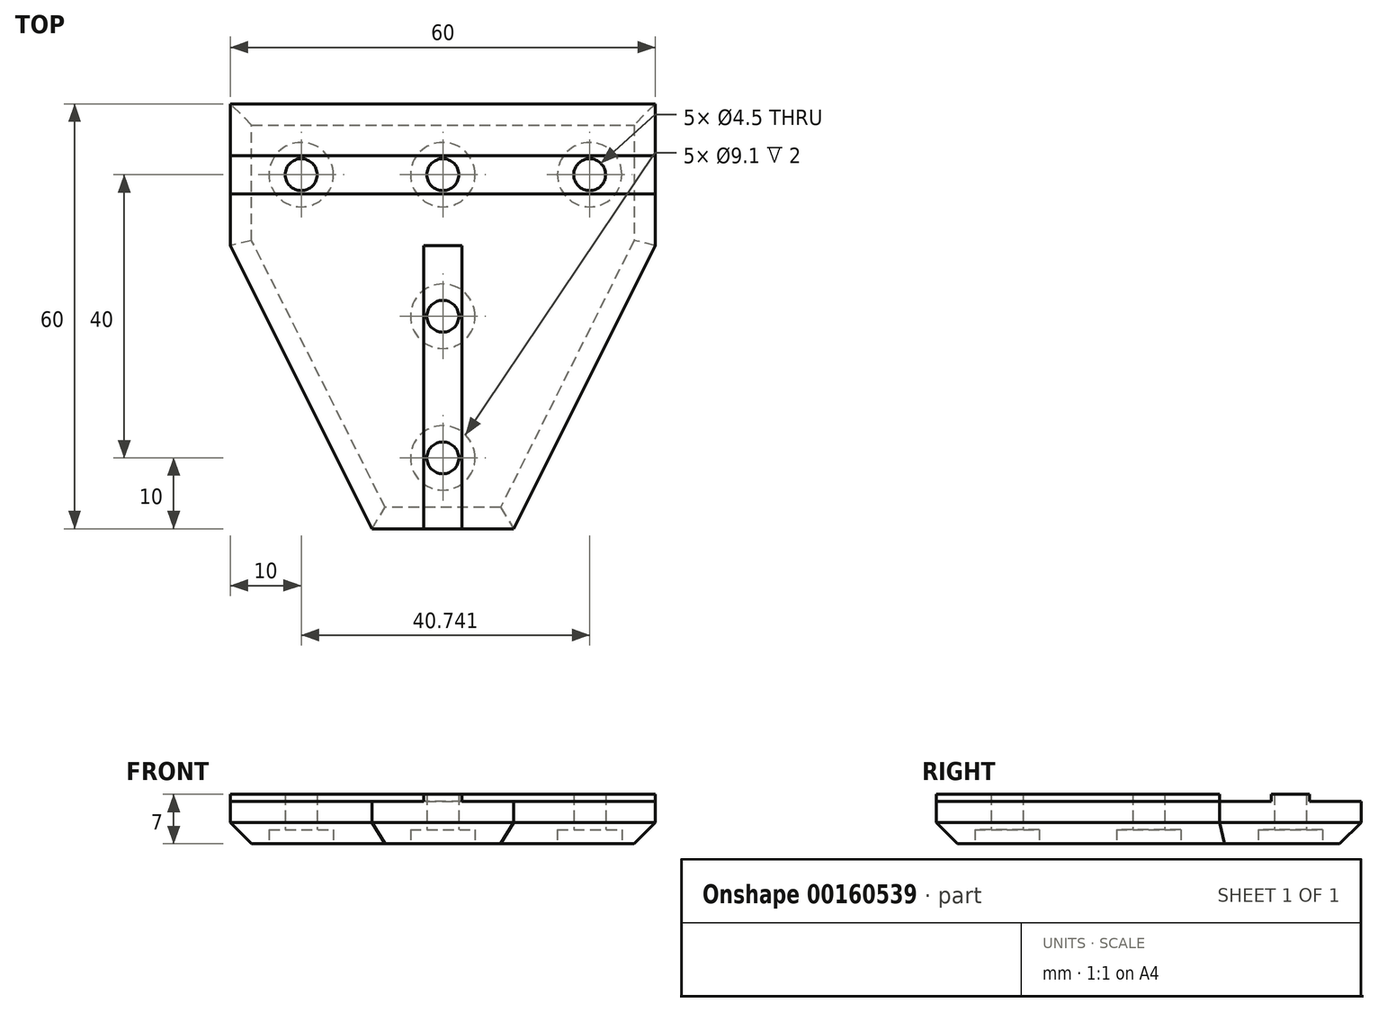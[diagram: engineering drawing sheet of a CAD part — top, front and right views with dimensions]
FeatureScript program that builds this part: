
annotation { "Feature Type Name" : "Feature", "Feature Type Description" : "" }
export const myFeature = defineFeature(function(context is Context, id is Id, definition is map)
    precondition{}
    {
        {
            var Q0;
            Q0=qCreatedBy(makeId("Top.planeOp"),FACE);
            var sketch = newSketch(context, id + "F0", { "sketchPlane" : qUnion([Q0])});
            skLineSegment(sketch, "E0", {"start": v(0, 0) * mm, "end": v(0, 20) * mm, "construction": true});
            skLineSegment(sketch, "E1", {"start": v(0, 0) * mm, "end": v(0, -40) * mm, "construction": true});
            skLineSegment(sketch, "E2", {"start": v(-10, 0) * mm, "end": v(-30, 0) * mm});
            skLineSegment(sketch, "E3", {"start": v(0, 20) * mm, "end": v(-30, 20) * mm});
            skLineSegment(sketch, "E4", {"start": v(-30, 20) * mm, "end": v(-30, 0) * mm});
            skLineSegment(sketch, "E5", {"start": v(0, 20) * mm, "end": v(30, 20) * mm});
            skLineSegment(sketch, "E6", {"start": v(30, 20) * mm, "end": v(30, 0) * mm});
            skLineSegment(sketch, "E7", {"start": v(30, 0) * mm, "end": v(10, 0) * mm});
            skLineSegment(sketch, "E8", {"start": v(0, -40) * mm, "end": v(10, -40) * mm});
            skLineSegment(sketch, "E9", {"start": v(10, -40) * mm, "end": v(10, 0) * mm});
            skLineSegment(sketch, "E10", {"start": v(0, -40) * mm, "end": v(-10, -40) * mm});
            skLineSegment(sketch, "E11", {"start": v(-10, -40) * mm, "end": v(-10, 0) * mm});
            skSolve(sketch);
        }
        {
            var Q0;
            Q0=qSketchRegion(id+"F0",true);
            extrude(context, id + "F1", {"entities" : qUnion([Q0]), "depth" : 6 * mm});
        }
        {
            var Q0;
            Q0=makeQuery(id+"F1.opExtrude","CAP_FACE",FACE,{"disambiguationData":[OSD([sQuery(id+"F0.wireOp",EDGE,"E2"),sQuery(id+"F0.wireOp",EDGE,"E3"),sQuery(id+"F0.wireOp",EDGE,"E4"),sQuery(id+"F0.wireOp",EDGE,"E5"),sQuery(id+"F0.wireOp",EDGE,"E6"),sQuery(id+"F0.wireOp",EDGE,"E7"),sQuery(id+"F0.wireOp",EDGE,"E8"),sQuery(id+"F0.wireOp",EDGE,"E9"),sQuery(id+"F0.wireOp",EDGE,"E10"),sQuery(id+"F0.wireOp",EDGE,"E11")])],"isStart":false});
            var sketch = newSketch(context, id + "F2", { "sketchPlane" : qUnion([Q0])});
            skLineSegment(sketch, "E12", {"start": v(-30, 10) * mm, "end": v(30, 10) * mm, "construction": true});
            skLineSegment(sketch, "E13", {"start": v(0, -40) * mm, "end": v(0, 0) * mm, "construction": true});
            skLineSegment(sketch, "E14", {"start": v(0, 0) * mm, "end": v(-2.71, 0) * mm});
            skLineSegment(sketch, "E15", {"start": v(-2.71, 0) * mm, "end": v(-2.7, -40) * mm});
            skLineSegment(sketch, "E16", {"start": v(2.71, -40) * mm, "end": v(2.71, 0) * mm});
            skLineSegment(sketch, "E17", {"start": v(2.71, 0) * mm, "end": v(0, 0) * mm});
            skLineSegment(sketch, "E18", {"start": v(-2.7, -40) * mm, "end": v(2.71, -40) * mm});
            skLineSegment(sketch, "E19", {"start": v(30, 12.71) * mm, "end": v(30, 7.3) * mm});
            skLineSegment(sketch, "E20", {"start": v(-30, 7.29) * mm, "end": v(30, 7.3) * mm});
            skLineSegment(sketch, "E21", {"start": v(-30, 7.29) * mm, "end": v(-30, 10) * mm});
            skLineSegment(sketch, "E22", {"start": v(-30, 10) * mm, "end": v(-30, 12.71) * mm});
            skLineSegment(sketch, "E23", {"start": v(-30, 12.71) * mm, "end": v(30, 12.71) * mm});
            skSolve(sketch);
        }
        {
            var Q0;
            Q0=qSketchRegion(id+"F2",true);
            extrude(context, id + "F3", {"entities" : qUnion([Q0]), "operationType" : NewBodyOperationType.ADD, "flatOperationType" : FlatOperationType.REMOVE, "offsetDistance" : 25 * mm, "depth" : 1 * mm, "domain" : OperationDomain.MODEL});
        }
        {
            var Q0;
            Q0=makeQuery(id+"F1.opExtrude","CAP_FACE",FACE,{"disambiguationData":[OSD([sQuery(id+"F0.wireOp",EDGE,"E2"),sQuery(id+"F0.wireOp",EDGE,"E3"),sQuery(id+"F0.wireOp",EDGE,"E4"),sQuery(id+"F0.wireOp",EDGE,"E5"),sQuery(id+"F0.wireOp",EDGE,"E6"),sQuery(id+"F0.wireOp",EDGE,"E7"),sQuery(id+"F0.wireOp",EDGE,"E8"),sQuery(id+"F0.wireOp",EDGE,"E9"),sQuery(id+"F0.wireOp",EDGE,"E10"),sQuery(id+"F0.wireOp",EDGE,"E11")])],"isStart":true});
            var sketch = newSketch(context, id + "F4", { "sketchPlane" : qUnion([Q0])});
            skCircle(sketch, "E24", {"center": v(-20, -10) * mm, "radius": 2.25 * mm});
            skCircle(sketch, "E25", {"center": v(0, 10) * mm, "radius": 2.25 * mm});
            skCircle(sketch, "E26", {"center": v(0, 30) * mm, "radius": 2.25 * mm});
            skCircle(sketch, "E27", {"center": v(20.74, -10) * mm, "radius": 2.25 * mm});
            skCircle(sketch, "E28", {"center": v(0, -10) * mm, "radius": 2.25 * mm});
            skSolve(sketch);
        }
        {
            var Q0;
            Q0=qSketchRegion(id+"F4",true);
            extrude(context, id + "F5", {"entities" : qUnion([Q0]), "operationType" : NewBodyOperationType.REMOVE, "endBound" : BoundingType.THROUGH_ALL, "oppositeDirection" : true, "depth" : 25 * mm});
        }
        {
            var Q0;
            Q0=makeQuery(id+"F1.opExtrude","CAP_FACE",FACE,{"disambiguationData":[OSD([sQuery(id+"F0.wireOp",EDGE,"E2"),sQuery(id+"F0.wireOp",EDGE,"E3"),sQuery(id+"F0.wireOp",EDGE,"E4"),sQuery(id+"F0.wireOp",EDGE,"E5"),sQuery(id+"F0.wireOp",EDGE,"E6"),sQuery(id+"F0.wireOp",EDGE,"E7"),sQuery(id+"F0.wireOp",EDGE,"E8"),sQuery(id+"F0.wireOp",EDGE,"E9"),sQuery(id+"F0.wireOp",EDGE,"E10"),sQuery(id+"F0.wireOp",EDGE,"E11")])],"isStart":true});
            var sketch = newSketch(context, id + "F6", { "sketchPlane" : qUnion([Q0])});
            skCircle(sketch, "E29", {"center": v(0, 30) * mm, "radius": 4.55 * mm});
            skCircle(sketch, "E30", {"center": v(0, 10) * mm, "radius": 4.55 * mm});
            skCircle(sketch, "E31", {"center": v(20.74, -10) * mm, "radius": 4.55 * mm});
            skCircle(sketch, "E32", {"center": v(-20, -10) * mm, "radius": 4.55 * mm});
            skCircle(sketch, "E33", {"center": v(0, -10) * mm, "radius": 4.55 * mm});
            skSolve(sketch);
        }
        {
            var Q0;
            Q0=qSketchRegion(id+"F6",true);
            extrude(context, id + "F7", {"entities" : qUnion([Q0]), "operationType" : NewBodyOperationType.REMOVE, "oppositeDirection" : true, "depth" : 2 * mm});
        }
        {
            var Q0;
            Q0=makeQuery(id+"F1.opExtrude","CAP_FACE",FACE,{"disambiguationData":[OSD([sQuery(id+"F0.wireOp",EDGE,"E2"),sQuery(id+"F0.wireOp",EDGE,"E3"),sQuery(id+"F0.wireOp",EDGE,"E4"),sQuery(id+"F0.wireOp",EDGE,"E5"),sQuery(id+"F0.wireOp",EDGE,"E6"),sQuery(id+"F0.wireOp",EDGE,"E7"),sQuery(id+"F0.wireOp",EDGE,"E8"),sQuery(id+"F0.wireOp",EDGE,"E9"),sQuery(id+"F0.wireOp",EDGE,"E10"),sQuery(id+"F0.wireOp",EDGE,"E11")])],"isStart":true});
            var sketch = newSketch(context, id + "F8", { "sketchPlane" : qUnion([Q0])});
            skLineSegment(sketch, "E34", {"start": v(-10, 40) * mm, "end": v(-30, 0) * mm});
            skLineSegment(sketch, "E35", {"start": v(-30, 0) * mm, "end": v(-10, 0) * mm});
            skLineSegment(sketch, "E36", {"start": v(-10, 0) * mm, "end": v(-10, 40) * mm});
            skLineSegment(sketch, "E37", {"start": v(10, 40) * mm, "end": v(10, 0) * mm});
            skLineSegment(sketch, "E38", {"start": v(10, 0) * mm, "end": v(30, 0) * mm});
            skLineSegment(sketch, "E39", {"start": v(30, 0) * mm, "end": v(10, 40) * mm});
            skSolve(sketch);
        }
        {
            var Q0;
            Q0 = qSketchRegion(id + "F8", true);
            extrude(context, id + "F9", {"entities" : qUnion([Q0]), "operationType" : NewBodyOperationType.ADD, "oppositeDirection" : true, "depth" : 6 * mm});
        }
        {
            var Q0;
            Q0=makeQuery(id+"F1.opExtrude","CAP_EDGE",EDGE,{"disambiguationData":[OSD([sQuery(id+"F0.wireOp",EDGE,"E8"),sQuery(id+"F0.wireOp",EDGE,"E10")])],"isStart":true});
            var Q1;
            Q1=makeQuery(id+"F9.opExtrude","CAP_EDGE",EDGE,{"disambiguationData":[OSD([sQuery(id+"F8.wireOp",EDGE,"E34")])],"isStart":true});
            var Q2;
            Q2=makeQuery(id+"F9.opExtrude","CAP_EDGE",EDGE,{"disambiguationData":[OSD([sQuery(id+"F8.wireOp",EDGE,"E39")])],"isStart":true});
            var Q3;
            Q3=makeQuery(id+"F1.opExtrude","CAP_EDGE",EDGE,{"disambiguationData":[OSD([sQuery(id+"F0.wireOp",EDGE,"E6")])],"isStart":true});
            var Q4;
            Q4=makeQuery(id+"F1.opExtrude","CAP_EDGE",EDGE,{"disambiguationData":[OSD([sQuery(id+"F0.wireOp",EDGE,"E3"),sQuery(id+"F0.wireOp",EDGE,"E5")])],"isStart":true});
            var Q5;
            Q5=makeQuery(id+"F1.opExtrude","CAP_EDGE",EDGE,{"disambiguationData":[OSD([sQuery(id+"F0.wireOp",EDGE,"E4")])],"isStart":true});
            chamfer(context, id + "F10", {"entities" : qUnion([Q0, Q1, Q2, Q3, Q4, Q5]), "width" : 3 * mm, "tangentPropagation" : true});
        }
    });
